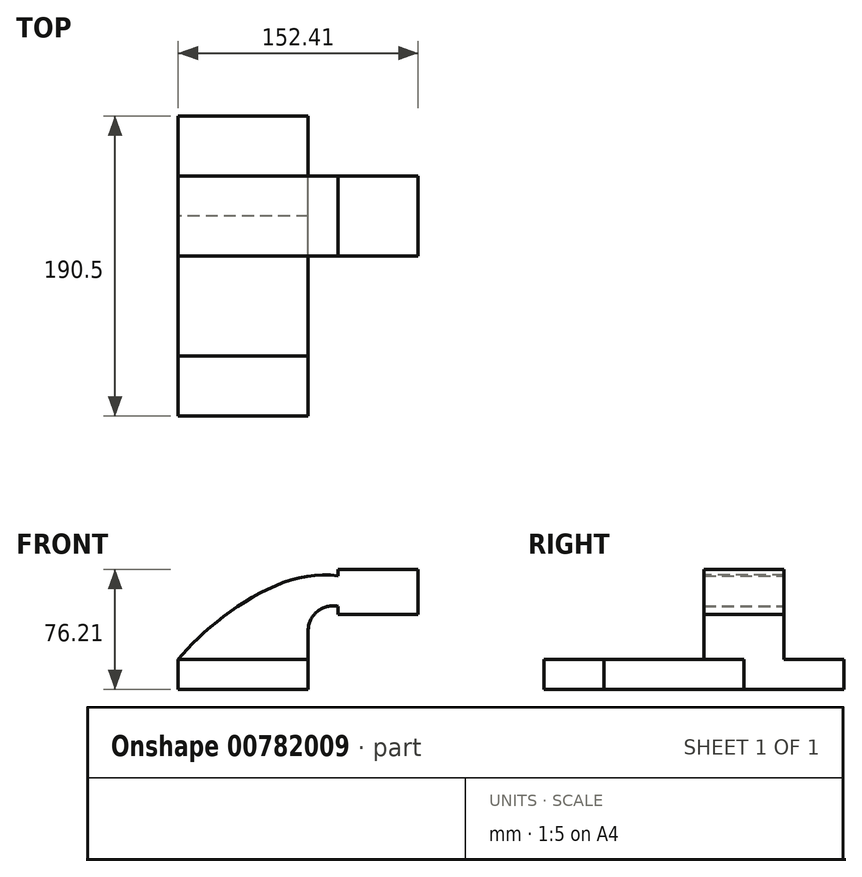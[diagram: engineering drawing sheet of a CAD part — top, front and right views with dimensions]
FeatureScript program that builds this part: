
annotation { "Feature Type Name" : "Feature", "Feature Type Description" : "" }
export const myFeature = defineFeature(function(context is Context, id is Id, definition is map)
    precondition{}
    {
        {
            var Q0;
            Q0=qCreatedBy(makeId("Front.planeOp"),FACE);
            var sketch = newSketch(context, id + "F0", { "sketchPlane" : qUnion([Q0])});
            skLineSegment(sketch, "E0.bottom", {"start": v(41.27, 9.53) * mm, "end": v(-41.28, 9.53) * mm});
            skLineSegment(sketch, "E0.top", {"start": v(41.28, -9.52) * mm, "end": v(-41.27, -9.52) * mm});
            skLineSegment(sketch, "E0.left", {"start": v(41.28, 9.53) * mm, "end": v(41.28, -9.52) * mm});
            skLineSegment(sketch, "E0.right", {"start": v(-41.28, 9.53) * mm, "end": v(-41.27, -9.52) * mm});
            skPoint(sketch, "E0.middle", {"position": v(0, 0) * mm});
            skLineSegment(sketch, "E1.bottom", {"start": v(111.12, 66.68) * mm, "end": v(60.33, 66.68) * mm});
            skLineSegment(sketch, "E1.top", {"start": v(111.12, 38.1) * mm, "end": v(60.33, 38.1) * mm});
            skLineSegment(sketch, "E1.left", {"start": v(111.12, 66.68) * mm, "end": v(111.12, 38.1) * mm});
            skLineSegment(sketch, "E1.right", {"start": v(60.33, 66.68) * mm, "end": v(60.33, 38.1) * mm});
            skPoint(sketch, "E1.middle", {"position": v(85.73, 52.39) * mm});
            skLineSegment(sketch, "E2", {"start": v(41.27, 9.53) * mm, "end": v(41.27, 27.75) * mm});
            skArc(sketch, "E3", {"start": v(41.27, 27.75) * mm, "mid": v(47.78, 40.56) * mm, "end": v(61.96, 42.88) * mm});
            skLineSegment(sketch, "E4", {"start": v(61.96, 42.88) * mm, "end": v(85.73, 42.88) * mm});
            skLineSegment(sketch, "E5.0", {"start": v(64.34, 61.93) * mm, "end": v(85.73, 61.93) * mm});
            skArc(sketch, "E5.1", {"start": v(22.23, 27.75) * mm, "mid": v(35.14, 54.87) * mm, "end": v(64.34, 61.93) * mm});
            skLineSegment(sketch, "E5.2", {"start": v(22.22, 9.53) * mm, "end": v(22.22, 27.75) * mm});
            skLineSegment(sketch, "E6", {"start": v(85.73, 42.88) * mm, "end": v(85.73, 61.93) * mm});
            skFitSpline(sketch, "E7", {"points": [v(-41.28, 9.53) * mm, v(64.34, 61.93) * mm], "startDerivative": vector(65.1, 77.65) * mm, "endDerivative": vector(114.32, -27.06) * mm});
            skSolve(sketch);
        }
        {
            var Q0;
            Q0=makeQuery(id+"F0.imprint","IMPRINT",FACE,{"disambiguationData":[TD([[makeQuery(id+"F0.imprint","IMPRINT",EDGE,{"derivedFrom":sQuery(id+"F0.wireOp",EDGE,"E0.top")}),-1.0]])]});
            extrude(context, id + "F1", {"entities" : qUnion([Q0]), "endBound" : BoundingType.SYMMETRIC, "depth" : 127 * mm, "offsetDistance" : 25.4 * mm});
        }
        {
            var Q0;
            Q0 = qSketchRegion(id + "F0", true);
            var Q1;
            Q1=makeQuery(id+"F1.opExtrude","CAP_FACE",FACE,{"disambiguationData":[OSD([sQuery(id+"F0.wireOp",EDGE,"E0.bottom"),sQuery(id+"F0.wireOp",EDGE,"E0.top"),sQuery(id+"F0.wireOp",EDGE,"E0.left"),sQuery(id+"F0.wireOp",EDGE,"E0.right")])],"isStart":false});
            extrude(context, id + "F2", {"entities" : qUnion([Q0, Q1]), "operationType" : NewBodyOperationType.ADD, "endBound" : BoundingType.SYMMETRIC, "depth" : 50.8 * mm, "offsetDistance" : 25.4 * mm});
        }
        {
            var Q0;
            Q0=makeQuery(id+"F0.imprint","IMPRINT",FACE,{"disambiguationData":[TD([[makeQuery(id+"F0.imprint","IMPRINT",EDGE,{"derivedFrom":sQuery(id+"F0.wireOp",EDGE,"E0.top")}),-1.0]])]});
            extrude(context, id + "F3", {"entities" : qUnion([Q0]), "depth" : 127 * mm, "offsetDistance" : 25.4 * mm});
        }
    });
